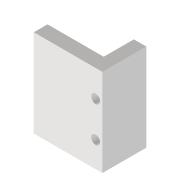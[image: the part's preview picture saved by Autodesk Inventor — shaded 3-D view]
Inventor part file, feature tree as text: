
AUTODESK INVENTOR PART (.ipt)
format: ipt  version: 2022 (Build 260153000, 153)  size: 104,960 bytes
history: native  units: mm
features: reference x11, other x4, extrude x2, sketch x2, plane x1
ambient origin geometry x8: Origin, YZ Plane, XZ Plane, XY Plane, X Axis, Y Axis, Z Axis, Center Point
bodies: Solid1 (feature_tree)
feature tree (20):
  extrude  "Extrusion1"  Depth=25.0mm
  sketch  "Sketch2"  dims[d2=3.3mm d3=5.0mm d4=0.0mm d5=5.0mm d6=0.0mm]
  plane  "Work Plane1"
  extrude  "Extrusion2"  Depth=5.0mm TaperAngle=0.0deg
  sketch  "Sketch1"  dims[d0=25.0mm d1=3.3mm]
  reference  "Reference1"
  reference  "Reference2"
  reference  "Reference3"
  reference  "Reference4"
  reference  "Reference5"
  reference  "Reference6"
  reference  "Reference7"
  reference  "Reference8"
  reference  "Reference9"
  reference  "Reference10"
  reference  "Reference11"
  other  "<userpath>\Documents\Inventor\Guinardia\INVENTOR\Assembly_Guinardia_V0.iam"
  other  "Assembly_Guinardia_V0.iam"
  other  "10_Wellplate_base:1"
  other  "00_NEMA8:1"
